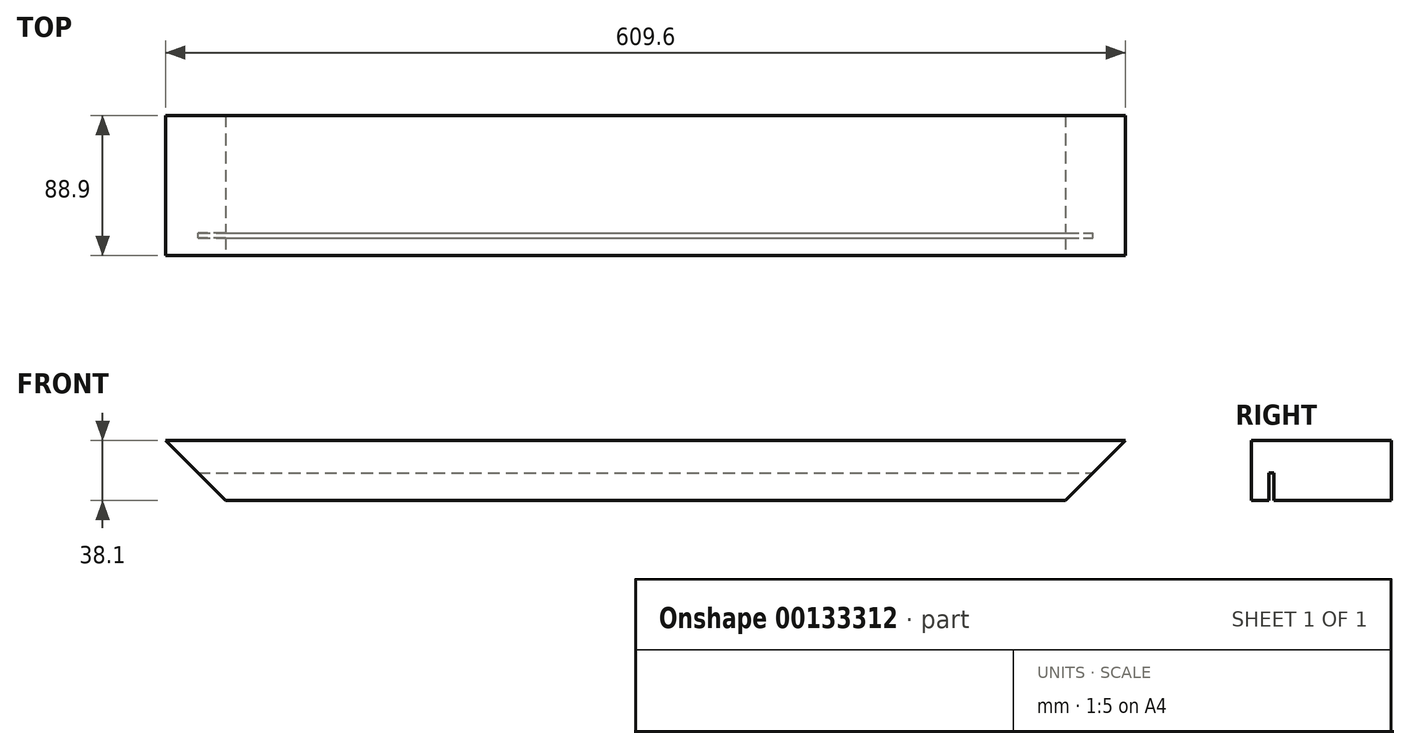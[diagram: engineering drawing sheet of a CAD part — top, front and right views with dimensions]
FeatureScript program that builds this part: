
annotation { "Feature Type Name" : "Feature", "Feature Type Description" : "" }
export const myFeature = defineFeature(function(context is Context, id is Id, definition is map)
    precondition{}
    {
        {
            var Q0;
            Q0=qCreatedBy(makeId("Top.planeOp"),FACE);
            var sketch = newSketch(context, id + "F0", { "sketchPlane" : qUnion([Q0])});
            skLineSegment(sketch, "E0.bottom", {"start": v(304.8, 44.45) * mm, "end": v(-304.8, 44.45) * mm});
            skLineSegment(sketch, "E0.top", {"start": v(304.8, -44.45) * mm, "end": v(-304.8, -44.45) * mm});
            skLineSegment(sketch, "E0.left", {"start": v(304.8, 44.45) * mm, "end": v(304.8, -44.45) * mm});
            skLineSegment(sketch, "E0.right", {"start": v(-304.8, 44.45) * mm, "end": v(-304.8, -44.45) * mm});
            skPoint(sketch, "E0.middle", {"position": v(0, 0) * mm});
            skSolve(sketch);
        }
        {
            var Q0;
            Q0=makeQuery(id+"F0.imprint","IMPRINT",FACE,{"disambiguationData":[TD([[makeQuery(id+"F0.imprint","IMPRINT",EDGE,{"derivedFrom":sQuery(id+"F0.wireOp",EDGE,"E0.bottom")}),1.0]])]});
            extrude(context, id + "F2", {"entities" : qUnion([Q0]), "depth" : 38.1 * mm});
        }
        {
            var Q0;
            Q0=makeQuery(id+"F2.opExtrude","SWEPT_FACE",FACE,{"disambiguationData":[OSD([sQuery(id+"F0.wireOp",EDGE,"E0.top")])]});
            var sketch = newSketch(context, id + "F3", { "sketchPlane" : qUnion([Q0])});
            skLineSegment(sketch, "E1.0", {"start": v(-304.8, 38.1) * mm, "end": v(-304.8, 0) * mm});
            skLineSegment(sketch, "E2.0", {"start": v(-266.7, 0) * mm, "end": v(-304.8, 0) * mm});
            skLineSegment(sketch, "E3", {"start": v(-266.7, 0) * mm, "end": v(-304.8, 38.1) * mm});
            skLineSegment(sketch, "E4", {"start": v(-304.8, 38.1) * mm, "end": v(-304.8, 38.1) * mm});
            skPoint(sketch, "E5.orphan", {"position": v(304.8, 0) * mm});
            skPoint(sketch, "E6.endSnap0", {"position": v(0, 38.1) * mm});
            skPoint(sketch, "E6.start.orphan", {"position": v(0, 38.1) * mm});
            skPoint(sketch, "E7.start.orphan", {"position": v(0, -16.72) * mm});
            skLineSegment(sketch, "E8", {"start": v(0, 38.1) * mm, "end": v(0, 0) * mm, "construction": true});
            skLineSegment(sketch, "E9.MirrorCS", {"start": v(266.7, 0) * mm, "end": v(304.8, 38.1) * mm});
            skLineSegment(sketch, "E10.MirrorCS", {"start": v(304.8, 38.1) * mm, "end": v(304.8, 0) * mm});
            skSolve(sketch);
        }
        {
            var Q0;
            Q0=makeQuery(id+"F3.imprint","IMPRINT",FACE,{"disambiguationData":[TD([[makeQuery(id+"F3.imprint","IMPRINT",EDGE,{"derivedFrom":sQuery(id+"F3.wireOp",EDGE,"E1.0")}),1.0]])]});
            var Q1;
            {var subQ0=sQuery(id+"F3.wireOp",EDGE,"E9.MirrorCS");Q1=makeQuery(id+"F3.imprint","IMPRINT",FACE,{"disambiguationData":[TD([[makeQuery(id+"F3.imprint","IMPRINT",EDGE,{"derivedFrom":subQ0}),-1.0]])]});}
            extrude(context, id + "F4", {"entities" : qUnion([Q0, Q1]), "operationType" : NewBodyOperationType.REMOVE, "endBound" : BoundingType.THROUGH_ALL, "oppositeDirection" : true, "depth" : 25.4 * mm});
        }
        {
            var Q0;
            Q0=makeQuery(id+"F2.opExtrude","CAP_FACE",FACE,{"disambiguationData":[OSD([sQuery(id+"F0.wireOp",EDGE,"E0.bottom"),sQuery(id+"F0.wireOp",EDGE,"E0.top"),sQuery(id+"F0.wireOp",EDGE,"E0.left"),sQuery(id+"F0.wireOp",EDGE,"E0.right")])],"isStart":true});
            var sketch = newSketch(context, id + "F5", { "sketchPlane" : qUnion([Q0])});
            skLineSegment(sketch, "E11.bottom", {"start": v(-304.8, 30.16) * mm, "end": v(304.8, 30.16) * mm});
            skLineSegment(sketch, "E11.top", {"start": v(-304.8, 33.34) * mm, "end": v(304.8, 33.34) * mm});
            skLineSegment(sketch, "E11.left", {"start": v(-304.8, 30.16) * mm, "end": v(-304.8, 33.34) * mm});
            skLineSegment(sketch, "E11.right", {"start": v(304.8, 30.16) * mm, "end": v(304.8, 33.34) * mm});
            skSolve(sketch);
        }
        {
            var Q0;
            {var subQ0=sQuery(id+"F5.wireOp",EDGE,"E11.right");Q0=makeQuery(id+"F5.imprint","IMPRINT",FACE,{"disambiguationData":[TD([[makeQuery(id+"F5.imprint","IMPRINT",EDGE,{"derivedFrom":subQ0}),1.0]])]});}
            var Q1;
            {var subQ0=sQuery(id+"F5.wireOp",EDGE,"E11.bottom");var subQ1=sQuery(id+"F0.wireOp",EDGE,"E0.top");var subQ4=makeQuery(id+"F4.boolean.opBoolean","COPY",EDGE,{"derivedFrom":makeQuery(id+"F4.opExtrude","SWEPT_EDGE",EDGE,{"disambiguationData":[OSD([subQ1,sQuery(id+"F3.wireOp",EDGE,"E9.MirrorCS")])]})});var subQ5=makeQuery(id+"F5.imprint","INTERSECT",VERTEX,{"derivedFrom":[subQ4,subQ0]});Q1=makeQuery(id+"F5.imprint","IMPRINT",FACE,{"disambiguationData":[TD([[makeQuery(id+"F5.imprint","IMPRINT",EDGE,{"disambiguationData":[TD([[subQ5,1.0]])],"derivedFrom":subQ0}),1.0]])]});}
            var Q2;
            {var subQ0=sQuery(id+"F5.wireOp",EDGE,"E11.left");Q2=makeQuery(id+"F5.imprint","IMPRINT",FACE,{"disambiguationData":[TD([[makeQuery(id+"F5.imprint","IMPRINT",EDGE,{"derivedFrom":subQ0}),-1.0]])]});}
            extrude(context, id + "F1", {"entities" : qUnion([Q0, Q1, Q2]), "operationType" : NewBodyOperationType.REMOVE, "oppositeDirection" : true, "depth" : 17.46 * mm});
        }
    });
